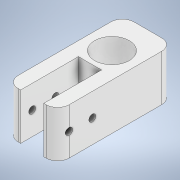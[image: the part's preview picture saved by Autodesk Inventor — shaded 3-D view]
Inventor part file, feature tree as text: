
AUTODESK INVENTOR PART (.ipt)
format: ipt  version: 2022 (Build 260153000, 153)  size: 146,432 bytes
history: native  units: mm
features: sketch x4, extrude x2, hole x2, other x1, fillet x1
ambient origin geometry x8: Origin, YZ Plane, XZ Plane, XY Plane, X Axis, Y Axis, Z Axis, Center Point
bodies: Body1 (feature_tree)
feature tree (10):
  other  "Sólido1"
  extrude  "Extrusão1"  Depth=20.0mm
  hole  "Furo1"  [1 undecoded]
  fillet  "Arredondamento1"  Radius=11.0mm
  extrude  "Extrusão2"  Depth=10.0mm
  hole  "Furo3"  [1 undecoded]
  sketch  "Esboço1"  dims[d0=22.0mm d1=20.0mm]
  sketch  "Esboço2"  dims[d2=50.0mm d3=0.0mm]
  sketch  "Esboço4"  dims[d4=15.0mm d5=6.0mm d6=4.0mm d7=2.0mm d8=90.0deg d9=8.0mm d10=20.594885mm d18=5.0mm d20=11.0mm]
  sketch  "Esboço5"  dims[d22=25.0mm d23=10.0mm d24=0.0mm d25=0.0mm d26=3.0mm d27=6.0mm d28=4.0mm d29=2.0mm d30=90.0deg d31=8.0mm d32=20.594885mm d33=5.0mm d34=10.0mm d35=34.49725mm]
note: 2 required parameter values undecoded (feature->parameter linkage not recoverable at this tier; creation-order binding heuristic only, values carry confidence <= 0.55)
